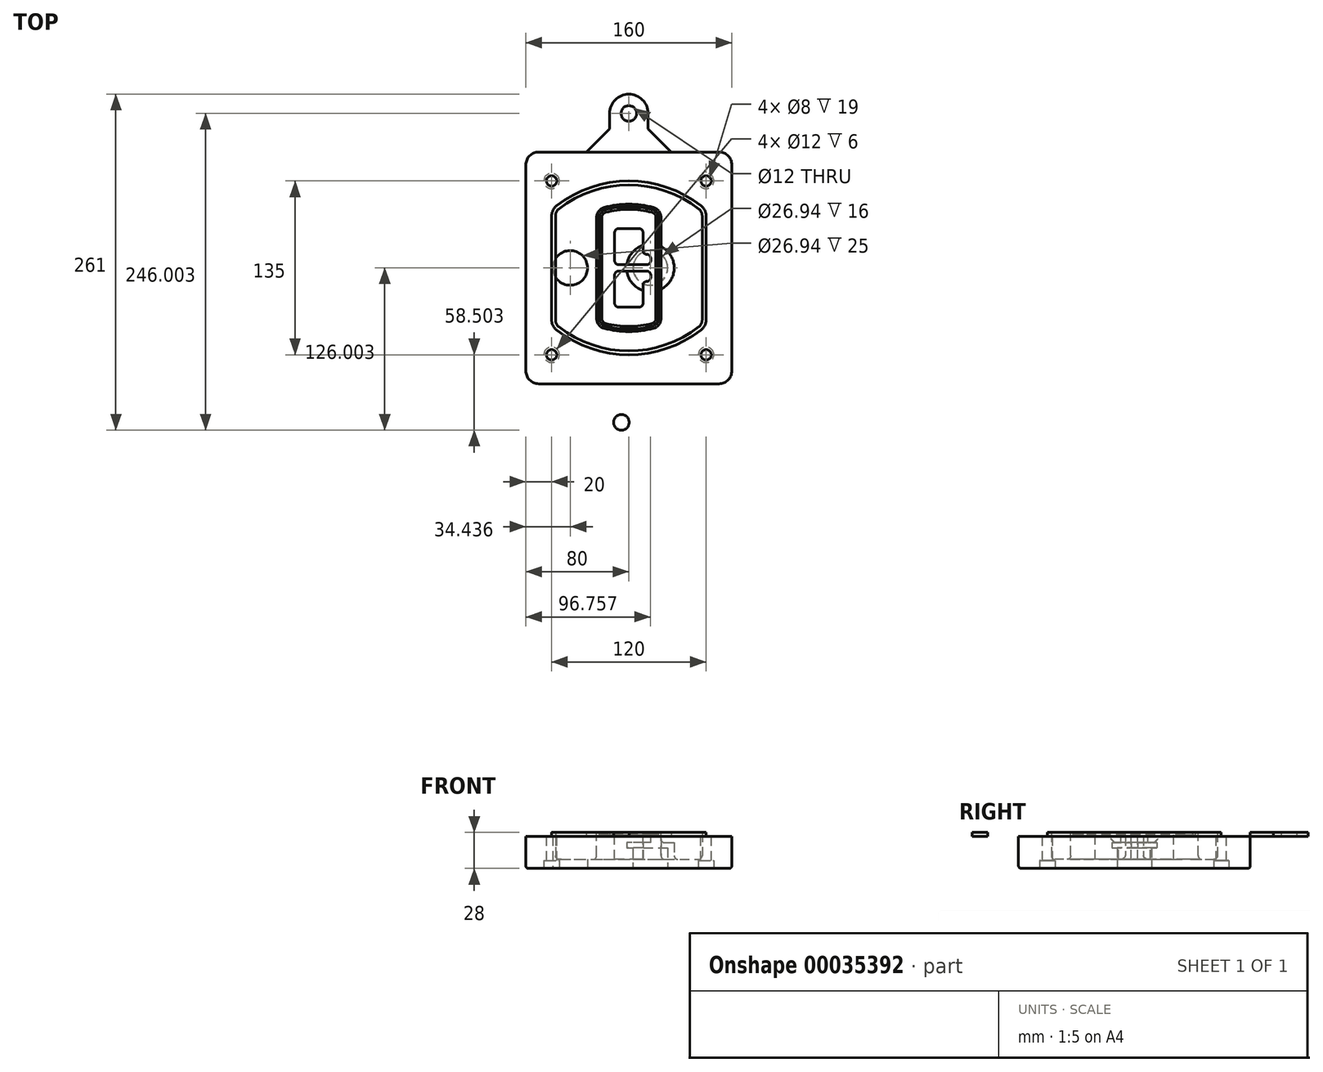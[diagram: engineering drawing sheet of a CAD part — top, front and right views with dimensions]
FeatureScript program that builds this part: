
annotation { "Feature Type Name" : "Feature", "Feature Type Description" : "" }
export const myFeature = defineFeature(function(context is Context, id is Id, definition is map)
    precondition{}
    {
        {
            var Q0;
            Q0=qCreatedBy(makeId("Top.planeOp"),FACE);
            var sketch = newSketch(context, id + "F0", { "sketchPlane" : qUnion([Q0])});
            skPoint(sketch, "E0.rect.middle", {"position": v(0, 0) * mm});
            skLineSegment(sketch, "E1.bottom", {"start": v(24.05, 28.38) * mm, "end": v(164.05, 28.38) * mm});
            skLineSegment(sketch, "E1.top", {"start": v(24.05, 208.38) * mm, "end": v(164.05, 208.38) * mm});
            skLineSegment(sketch, "E1.left", {"start": v(14.05, 38.38) * mm, "end": v(14.05, 198.38) * mm});
            skLineSegment(sketch, "E1.right", {"start": v(174.05, 38.38) * mm, "end": v(174.05, 198.38) * mm});
            skLineSegment(sketch, "E2", {"start": v(14.05, 208.38) * mm, "end": v(174.05, 28.38) * mm, "construction": true});
            skLineSegment(sketch, "E3", {"start": v(174.05, 208.38) * mm, "end": v(14.05, 28.38) * mm, "construction": true});
            skCircle(sketch, "E4", {"center": v(34.05, 185.88) * mm, "radius": 4 * mm});
            skCircle(sketch, "E5", {"center": v(154.05, 185.88) * mm, "radius": 4 * mm});
            skCircle(sketch, "E6", {"center": v(154.05, 50.88) * mm, "radius": 4 * mm});
            skCircle(sketch, "E7", {"center": v(34.05, 50.88) * mm, "radius": 4 * mm});
            skLineSegment(sketch, "E8", {"start": v(34.05, 185.88) * mm, "end": v(154.05, 185.88) * mm, "construction": true});
            skLineSegment(sketch, "E9", {"start": v(154.05, 185.88) * mm, "end": v(154.05, 50.88) * mm, "construction": true});
            skLineSegment(sketch, "E10", {"start": v(154.05, 50.88) * mm, "end": v(34.05, 50.88) * mm, "construction": true});
            skLineSegment(sketch, "E11", {"start": v(34.05, 50.88) * mm, "end": v(34.05, 185.88) * mm, "construction": true});
            skLineSegment(sketch, "E12", {"start": v(34.05, 158.68) * mm, "end": v(34.05, 78.09) * mm});
            skLineSegment(sketch, "E13", {"start": v(154.05, 158.68) * mm, "end": v(154.05, 78.09) * mm});
            skArc(sketch, "E14", {"start": v(150.2, 166.56) * mm, "mid": v(94.05, 185.88) * mm, "end": v(37.9, 166.56) * mm});
            skArc(sketch, "E15", {"start": v(37.9, 70.2) * mm, "mid": v(94.05, 50.88) * mm, "end": v(150.2, 70.2) * mm});
            skLineSegment(sketch, "E16", {"start": v(34.05, 118.38) * mm, "end": v(154.05, 118.38) * mm, "construction": true});
            skPoint(sketch, "E17.visualSharp", {"position": v(34.05, 73.38) * mm});
            skArc(sketch, "E17.filletArc", {"start": v(34.05, 78.09) * mm, "mid": v(35.06, 73.7) * mm, "end": v(37.9, 70.2) * mm});
            skPoint(sketch, "E18.visualSharp", {"position": v(34.05, 163.38) * mm});
            skArc(sketch, "E18.filletArc", {"start": v(37.9, 166.56) * mm, "mid": v(35.06, 163.06) * mm, "end": v(34.05, 158.68) * mm});
            skPoint(sketch, "E19.visualSharp", {"position": v(154.05, 163.38) * mm});
            skArc(sketch, "E19.filletArc", {"start": v(154.05, 158.68) * mm, "mid": v(153.04, 163.06) * mm, "end": v(150.2, 166.56) * mm});
            skPoint(sketch, "E20.visualSharp", {"position": v(154.05, 73.38) * mm});
            skArc(sketch, "E20.filletArc", {"start": v(150.2, 70.2) * mm, "mid": v(153.04, 73.7) * mm, "end": v(154.05, 78.09) * mm});
            skPoint(sketch, "E21.visualSharp", {"position": v(14.05, 208.38) * mm});
            skArc(sketch, "E21.filletArc", {"start": v(24.05, 208.38) * mm, "mid": v(16.98, 205.45) * mm, "end": v(14.05, 198.38) * mm});
            skPoint(sketch, "E22.visualSharp", {"position": v(174.05, 208.38) * mm});
            skArc(sketch, "E22.filletArc", {"start": v(174.05, 198.38) * mm, "mid": v(171.12, 205.45) * mm, "end": v(164.05, 208.38) * mm});
            skPoint(sketch, "E23.visualSharp", {"position": v(174.05, 28.38) * mm});
            skArc(sketch, "E23.filletArc", {"start": v(164.05, 28.38) * mm, "mid": v(171.12, 31.31) * mm, "end": v(174.05, 38.38) * mm});
            skPoint(sketch, "E24.visualSharp", {"position": v(14.05, 28.38) * mm});
            skArc(sketch, "E24.filletArc", {"start": v(14.05, 38.38) * mm, "mid": v(16.98, 31.31) * mm, "end": v(24.05, 28.38) * mm});
            skArc(sketch, "E25.0", {"start": v(151.05, 158.68) * mm, "mid": v(150.34, 161.75) * mm, "end": v(148.36, 164.2) * mm});
            skLineSegment(sketch, "E25.1", {"start": v(151.05, 158.68) * mm, "end": v(151.05, 78.09) * mm});
            skArc(sketch, "E25.2", {"start": v(148.36, 72.57) * mm, "mid": v(150.34, 75.02) * mm, "end": v(151.05, 78.09) * mm});
            skArc(sketch, "E25.3", {"start": v(39.74, 72.57) * mm, "mid": v(94.05, 53.88) * mm, "end": v(148.36, 72.57) * mm});
            skArc(sketch, "E25.4", {"start": v(37.05, 78.09) * mm, "mid": v(37.76, 75.02) * mm, "end": v(39.74, 72.57) * mm});
            skArc(sketch, "E25.5", {"start": v(148.36, 164.2) * mm, "mid": v(94.05, 182.88) * mm, "end": v(39.74, 164.2) * mm});
            skLineSegment(sketch, "E25.6", {"start": v(37.05, 158.68) * mm, "end": v(37.05, 78.09) * mm});
            skArc(sketch, "E25.7", {"start": v(39.74, 164.2) * mm, "mid": v(37.76, 161.75) * mm, "end": v(37.05, 158.68) * mm});
            skArc(sketch, "E26.0", {"start": v(35.43, 169.71) * mm, "mid": v(31.47, 164.82) * mm, "end": v(30.05, 158.68) * mm});
            skArc(sketch, "E26.1", {"start": v(152.67, 169.71) * mm, "mid": v(94.05, 189.88) * mm, "end": v(35.43, 169.71) * mm});
            skArc(sketch, "E26.2", {"start": v(158.05, 158.68) * mm, "mid": v(156.63, 164.82) * mm, "end": v(152.67, 169.71) * mm});
            skLineSegment(sketch, "E26.3", {"start": v(158.05, 158.68) * mm, "end": v(158.05, 78.09) * mm});
            skArc(sketch, "E26.4", {"start": v(152.67, 67.05) * mm, "mid": v(156.63, 71.95) * mm, "end": v(158.05, 78.09) * mm});
            skLineSegment(sketch, "E26.5", {"start": v(30.05, 158.68) * mm, "end": v(30.05, 78.09) * mm});
            skArc(sketch, "E26.6", {"start": v(35.43, 67.05) * mm, "mid": v(94.05, 46.88) * mm, "end": v(152.67, 67.05) * mm});
            skArc(sketch, "E26.7", {"start": v(30.05, 78.09) * mm, "mid": v(31.47, 71.95) * mm, "end": v(35.43, 67.05) * mm});
            skSolve(sketch);
        }
        {
            var Q0;
            Q0=makeQuery(id+"F0.imprint","IMPRINT",FACE,{"disambiguationData":[TD([[makeQuery(id+"F0.imprint","IMPRINT",EDGE,{"derivedFrom":sQuery(id+"F0.wireOp",EDGE,"E1.bottom")}),1.0]])]});
            var Q1;
            Q1=makeQuery(id+"F0.imprint","IMPRINT",FACE,{"disambiguationData":[TD([[makeQuery(id+"F0.imprint","IMPRINT",EDGE,{"derivedFrom":sQuery(id+"F0.wireOp",EDGE,"E12")}),1.0]])]});
            var Q2;
            Q2=makeQuery(id+"F0.imprint","IMPRINT",FACE,{"disambiguationData":[TD([[makeQuery(id+"F0.imprint","IMPRINT",EDGE,{"derivedFrom":sQuery(id+"F0.wireOp",EDGE,"E25.0")}),1.0]])]});
            var Q3;
            Q3=makeQuery(id+"F0.imprint","IMPRINT",FACE,{"disambiguationData":[TD([[makeQuery(id+"F0.imprint","IMPRINT",EDGE,{"derivedFrom":sQuery(id+"F0.wireOp",EDGE,"E12")}),-1.0]])]});
            extrude(context, id + "F1", {"entities" : qUnion([Q0, Q1, Q2, Q3]), "oppositeDirection" : true, "depth" : 25 * mm});
        }
        {
            var Q0;
            Q0=makeQuery(id+"F0.imprint","IMPRINT",FACE,{"disambiguationData":[TD([[makeQuery(id+"F0.imprint","IMPRINT",EDGE,{"derivedFrom":sQuery(id+"F0.wireOp",EDGE,"E12")}),1.0]])]});
            extrude(context, id + "F2", {"entities" : qUnion([Q0]), "operationType" : NewBodyOperationType.ADD, "depth" : 3 * mm});
        }
        {
            var Q0;
            Q0=makeQuery(id+"F0.imprint","IMPRINT",FACE,{"disambiguationData":[TD([[makeQuery(id+"F0.imprint","IMPRINT",EDGE,{"derivedFrom":sQuery(id+"F0.wireOp",EDGE,"E25.0")}),1.0]])]});
            extrude(context, id + "F3", {"entities" : qUnion([Q0]), "operationType" : NewBodyOperationType.REMOVE, "oppositeDirection" : true, "depth" : 18 * mm});
        }
        {
            var Q0;
            Q0=makeQuery(id+"F2.opExtrude","CAP_FACE",FACE,{"disambiguationData":[OSD([sQuery(id+"F0.wireOp",EDGE,"E12"),sQuery(id+"F0.wireOp",EDGE,"E13"),sQuery(id+"F0.wireOp",EDGE,"E14"),sQuery(id+"F0.wireOp",EDGE,"E15"),sQuery(id+"F0.wireOp",EDGE,"E17.filletArc"),sQuery(id+"F0.wireOp",EDGE,"E18.filletArc"),sQuery(id+"F0.wireOp",EDGE,"E19.filletArc"),sQuery(id+"F0.wireOp",EDGE,"E20.filletArc"),sQuery(id+"F0.wireOp",EDGE,"E25.0"),sQuery(id+"F0.wireOp",EDGE,"E25.1"),sQuery(id+"F0.wireOp",EDGE,"E25.2"),sQuery(id+"F0.wireOp",EDGE,"E25.3"),sQuery(id+"F0.wireOp",EDGE,"E25.4"),sQuery(id+"F0.wireOp",EDGE,"E25.5"),sQuery(id+"F0.wireOp",EDGE,"E25.6"),sQuery(id+"F0.wireOp",EDGE,"E25.7")])],"isStart":false});
            var sketch = newSketch(context, id + "F4", { "sketchPlane" : qUnion([Q0])});
            skArc(sketch, "E27.0", {"start": v(74.97, 71.41) * mm, "mid": v(94.05, 68.88) * mm, "end": v(113.13, 71.41) * mm});
            skArc(sketch, "E28.0", {"start": v(113.13, 165.35) * mm, "mid": v(94.05, 167.88) * mm, "end": v(74.97, 165.35) * mm});
            skLineSegment(sketch, "E29", {"start": v(69.05, 157.63) * mm, "end": v(69.05, 79.14) * mm});
            skLineSegment(sketch, "E30", {"start": v(119.05, 157.63) * mm, "end": v(119.05, 79.14) * mm});
            skLineSegment(sketch, "E31", {"start": v(69.05, 163.48) * mm, "end": v(119.05, 163.48) * mm, "construction": true});
            skLineSegment(sketch, "E32", {"start": v(69.05, 73.28) * mm, "end": v(119.05, 73.28) * mm, "construction": true});
            skPoint(sketch, "E33.visualSharp", {"position": v(69.05, 163.48) * mm});
            skArc(sketch, "E33.filletArc", {"start": v(74.97, 165.35) * mm, "mid": v(70.7, 162.5) * mm, "end": v(69.05, 157.63) * mm});
            skPoint(sketch, "E34.visualSharp", {"position": v(119.05, 163.48) * mm});
            skArc(sketch, "E34.filletArc", {"start": v(119.05, 157.63) * mm, "mid": v(117.4, 162.5) * mm, "end": v(113.13, 165.35) * mm});
            skPoint(sketch, "E35.visualSharp", {"position": v(119.05, 73.28) * mm});
            skArc(sketch, "E35.filletArc", {"start": v(113.13, 71.41) * mm, "mid": v(117.4, 74.27) * mm, "end": v(119.05, 79.14) * mm});
            skPoint(sketch, "E36.visualSharp", {"position": v(69.05, 73.28) * mm});
            skArc(sketch, "E36.filletArc", {"start": v(69.05, 79.14) * mm, "mid": v(70.7, 74.27) * mm, "end": v(74.97, 71.41) * mm});
            skArc(sketch, "E37.0", {"start": v(148.36, 164.2) * mm, "mid": v(94.05, 182.88) * mm, "end": v(39.74, 164.2) * mm});
            skArc(sketch, "E37.1", {"start": v(39.74, 164.2) * mm, "mid": v(37.76, 161.75) * mm, "end": v(37.05, 158.68) * mm});
            skLineSegment(sketch, "E37.2", {"start": v(37.05, 158.68) * mm, "end": v(37.05, 78.09) * mm});
            skArc(sketch, "E37.3", {"start": v(37.05, 78.09) * mm, "mid": v(37.76, 75.02) * mm, "end": v(39.74, 72.57) * mm});
            skArc(sketch, "E37.4", {"start": v(39.74, 72.57) * mm, "mid": v(94.05, 53.88) * mm, "end": v(148.36, 72.57) * mm});
            skArc(sketch, "E37.5", {"start": v(148.36, 72.57) * mm, "mid": v(150.34, 75.02) * mm, "end": v(151.05, 78.09) * mm});
            skLineSegment(sketch, "E37.6", {"start": v(151.05, 158.68) * mm, "end": v(151.05, 78.09) * mm});
            skArc(sketch, "E37.7", {"start": v(151.05, 158.68) * mm, "mid": v(150.34, 161.75) * mm, "end": v(148.36, 164.2) * mm});
            skLineSegment(sketch, "E38.0", {"start": v(117.05, 157.63) * mm, "end": v(117.05, 79.14) * mm});
            skArc(sketch, "E38.1", {"start": v(112.61, 73.34) * mm, "mid": v(115.81, 75.49) * mm, "end": v(117.05, 79.14) * mm});
            skArc(sketch, "E38.2", {"start": v(75.49, 73.34) * mm, "mid": v(94.05, 70.88) * mm, "end": v(112.61, 73.34) * mm});
            skArc(sketch, "E38.3", {"start": v(71.05, 79.14) * mm, "mid": v(72.29, 75.49) * mm, "end": v(75.49, 73.34) * mm});
            skLineSegment(sketch, "E38.4", {"start": v(71.05, 157.63) * mm, "end": v(71.05, 79.14) * mm});
            skArc(sketch, "E38.5", {"start": v(117.05, 157.63) * mm, "mid": v(115.81, 161.28) * mm, "end": v(112.61, 163.42) * mm});
            skArc(sketch, "E38.6", {"start": v(75.49, 163.42) * mm, "mid": v(72.29, 161.28) * mm, "end": v(71.05, 157.63) * mm});
            skArc(sketch, "E38.7", {"start": v(112.61, 163.42) * mm, "mid": v(94.05, 165.88) * mm, "end": v(75.49, 163.42) * mm});
            skArc(sketch, "E39.0", {"start": v(115.05, 157.63) * mm, "mid": v(114.23, 160.06) * mm, "end": v(112.1, 161.5) * mm});
            skLineSegment(sketch, "E39.1", {"start": v(115.05, 157.63) * mm, "end": v(115.05, 79.14) * mm});
            skArc(sketch, "E39.2", {"start": v(112.1, 75.27) * mm, "mid": v(114.23, 76.7) * mm, "end": v(115.05, 79.14) * mm});
            skArc(sketch, "E39.3", {"start": v(76, 75.27) * mm, "mid": v(94.05, 72.88) * mm, "end": v(112.1, 75.27) * mm});
            skArc(sketch, "E39.4", {"start": v(73.05, 79.14) * mm, "mid": v(73.87, 76.7) * mm, "end": v(76, 75.27) * mm});
            skArc(sketch, "E39.5", {"start": v(112.1, 161.5) * mm, "mid": v(94.05, 163.88) * mm, "end": v(76, 161.5) * mm});
            skLineSegment(sketch, "E39.6", {"start": v(73.05, 157.63) * mm, "end": v(73.05, 79.14) * mm});
            skArc(sketch, "E39.7", {"start": v(76, 161.5) * mm, "mid": v(73.87, 160.06) * mm, "end": v(73.05, 157.63) * mm});
            skLineSegment(sketch, "E40", {"start": v(69.05, 118.38) * mm, "end": v(119.05, 118.38) * mm, "construction": true});
            skLineSegment(sketch, "E41", {"start": v(83.05, 123.88) * mm, "end": v(83.05, 145.88) * mm});
            skLineSegment(sketch, "E42", {"start": v(86.05, 148.88) * mm, "end": v(102.05, 148.88) * mm});
            skLineSegment(sketch, "E43", {"start": v(105.05, 145.88) * mm, "end": v(105.05, 131.88) * mm});
            skLineSegment(sketch, "E44", {"start": v(108.05, 128.88) * mm, "end": v(108.05, 128.88) * mm});
            skLineSegment(sketch, "E45", {"start": v(111.05, 125.88) * mm, "end": v(111.05, 123.88) * mm});
            skLineSegment(sketch, "E46", {"start": v(108.05, 120.88) * mm, "end": v(86.05, 120.88) * mm});
            skPoint(sketch, "E47.visualSharp", {"position": v(83.05, 148.88) * mm});
            skArc(sketch, "E47.filletArc", {"start": v(86.05, 148.88) * mm, "mid": v(83.93, 148) * mm, "end": v(83.05, 145.88) * mm});
            skPoint(sketch, "E48.visualSharp", {"position": v(105.05, 148.88) * mm});
            skArc(sketch, "E48.filletArc", {"start": v(105.05, 145.88) * mm, "mid": v(104.17, 148) * mm, "end": v(102.05, 148.88) * mm});
            skPoint(sketch, "E49.visualSharp", {"position": v(105.05, 128.88) * mm});
            skArc(sketch, "E49.filletArc", {"start": v(105.05, 131.88) * mm, "mid": v(105.93, 129.76) * mm, "end": v(108.05, 128.88) * mm});
            skPoint(sketch, "E50.visualSharp", {"position": v(111.05, 128.88) * mm});
            skArc(sketch, "E50.filletArc", {"start": v(111.05, 125.88) * mm, "mid": v(110.17, 128) * mm, "end": v(108.05, 128.88) * mm});
            skPoint(sketch, "E51.visualSharp", {"position": v(111.05, 120.88) * mm});
            skArc(sketch, "E51.filletArc", {"start": v(108.05, 120.88) * mm, "mid": v(110.17, 121.76) * mm, "end": v(111.05, 123.88) * mm});
            skPoint(sketch, "E52.visualSharp", {"position": v(83.05, 120.88) * mm});
            skArc(sketch, "E52.filletArc", {"start": v(83.05, 123.88) * mm, "mid": v(83.93, 121.76) * mm, "end": v(86.05, 120.88) * mm});
            skLineSegment(sketch, "E53.0.MirrorCS", {"start": v(108.05, 115.88) * mm, "end": v(86.05, 115.88) * mm});
            skArc(sketch, "E54.0.MirrorCS", {"start": v(83.05, 112.88) * mm, "mid": v(83.93, 115) * mm, "end": v(86.05, 115.88) * mm});
            skLineSegment(sketch, "E55.0.MirrorCS", {"start": v(83.05, 112.88) * mm, "end": v(83.05, 90.88) * mm});
            skArc(sketch, "E56.0.MirrorCS", {"start": v(86.05, 87.88) * mm, "mid": v(83.93, 88.76) * mm, "end": v(83.05, 90.88) * mm});
            skLineSegment(sketch, "E57.0.MirrorCS", {"start": v(86.05, 87.88) * mm, "end": v(102.05, 87.88) * mm});
            skArc(sketch, "E58.0.MirrorCS", {"start": v(105.05, 90.88) * mm, "mid": v(104.17, 88.76) * mm, "end": v(102.05, 87.88) * mm});
            skLineSegment(sketch, "E59.0.MirrorCS", {"start": v(105.05, 90.88) * mm, "end": v(105.05, 104.88) * mm});
            skArc(sketch, "E60.0.MirrorCS", {"start": v(105.05, 104.88) * mm, "mid": v(105.93, 107) * mm, "end": v(108.05, 107.88) * mm});
            skArc(sketch, "E61.0.MirrorCS", {"start": v(111.05, 110.88) * mm, "mid": v(110.17, 108.76) * mm, "end": v(108.05, 107.88) * mm});
            skLineSegment(sketch, "E62.0.MirrorCS", {"start": v(111.05, 110.88) * mm, "end": v(111.05, 112.88) * mm});
            skArc(sketch, "E63.0.MirrorCS", {"start": v(108.05, 115.88) * mm, "mid": v(110.17, 115) * mm, "end": v(111.05, 112.88) * mm});
            skSolve(sketch);
        }
        {
            var Q0;
            Q0=makeQuery(id+"F4.imprint","IMPRINT",FACE,{"disambiguationData":[TD([[makeQuery(id+"F4.imprint","IMPRINT",EDGE,{"derivedFrom":sQuery(id+"F4.wireOp",EDGE,"E27.0")}),1.0]])]});
            var Q1;
            Q1=makeQuery(id+"F4.imprint","IMPRINT",FACE,{"disambiguationData":[TD([[makeQuery(id+"F4.imprint","IMPRINT",EDGE,{"derivedFrom":sQuery(id+"F4.wireOp",EDGE,"E38.0")}),-1.0]])]});
            var Q2;
            Q2=makeQuery(id+"F4.imprint","IMPRINT",FACE,{"disambiguationData":[TD([[makeQuery(id+"F4.imprint","IMPRINT",EDGE,{"derivedFrom":sQuery(id+"F4.wireOp",EDGE,"E39.0")}),1.0]])]});
            extrude(context, id + "F5", {"entities" : qUnion([Q0, Q1, Q2]), "operationType" : NewBodyOperationType.ADD, "endBound" : BoundingType.UP_TO_NEXT, "oppositeDirection" : true, "depth" : 25 * mm});
        }
        {
            var Q0;
            Q0=makeQuery(id+"F4.imprint","IMPRINT",FACE,{"disambiguationData":[TD([[makeQuery(id+"F4.imprint","IMPRINT",EDGE,{"derivedFrom":sQuery(id+"F4.wireOp",EDGE,"E38.0")}),-1.0]])]});
            extrude(context, id + "F6", {"entities" : qUnion([Q0]), "operationType" : NewBodyOperationType.REMOVE, "oppositeDirection" : true, "depth" : 2 * mm});
        }
        {
            var Q0;
            Q0=makeQuery(id+"F1.opExtrude","CAP_FACE",FACE,{"disambiguationData":[OSD([sQuery(id+"F0.wireOp",EDGE,"E1.bottom"),sQuery(id+"F0.wireOp",EDGE,"E1.top"),sQuery(id+"F0.wireOp",EDGE,"E1.left"),sQuery(id+"F0.wireOp",EDGE,"E1.right"),sQuery(id+"F0.wireOp",EDGE,"E4"),sQuery(id+"F0.wireOp",EDGE,"E5"),sQuery(id+"F0.wireOp",EDGE,"E6"),sQuery(id+"F0.wireOp",EDGE,"E7"),sQuery(id+"F0.wireOp",EDGE,"E21.filletArc"),sQuery(id+"F0.wireOp",EDGE,"E22.filletArc"),sQuery(id+"F0.wireOp",EDGE,"E23.filletArc"),sQuery(id+"F0.wireOp",EDGE,"E24.filletArc")])],"isStart":false});
            var sketch = newSketch(context, id + "F7", { "sketchPlane" : qUnion([Q0])});
            skCircle(sketch, "E64", {"center": v(110.8, -118.38) * mm, "radius": 13.47 * mm});
            skCircle(sketch, "E65", {"center": v(48.49, -118.38) * mm, "radius": 13.47 * mm});
            skLineSegment(sketch, "E66", {"start": v(174.05, -118.38) * mm, "end": v(14.05, -118.38) * mm});
            skCircle(sketch, "E67", {"center": v(110.8, -118.38) * mm, "radius": 18.47 * mm});
            skCircle(sketch, "E68", {"center": v(154.05, -185.88) * mm, "radius": 6 * mm});
            skCircle(sketch, "E69", {"center": v(34.05, -185.88) * mm, "radius": 6 * mm});
            skCircle(sketch, "E70", {"center": v(34.05, -50.88) * mm, "radius": 6 * mm});
            skCircle(sketch, "E71", {"center": v(154.05, -50.88) * mm, "radius": 6 * mm});
            skSolve(sketch);
        }
        {
            var Q0;
            {var subQ1=sQuery(id+"F7.wireOp",EDGE,"E66");var subQ4=sQuery(id+"F7.wireOp",EDGE,"E64");var subQ6=makeQuery(id+"F7.imprint","INTERSECT",VERTEX,{"disambiguationData":[OD(0.0)],"derivedFrom":[subQ4,subQ1]});Q0=makeQuery(id+"F7.imprint","IMPRINT",FACE,{"disambiguationData":[TD([[makeQuery(id+"F7.imprint","IMPRINT",EDGE,{"disambiguationData":[TD([[subQ6,-1.0]])],"derivedFrom":subQ4}),-1.0]])]});}
            var Q1;
            {var subQ0=sQuery(id+"F7.wireOp",EDGE,"E66");var subQ1=sQuery(id+"F7.wireOp",EDGE,"E64");var subQ3=makeQuery(id+"F7.imprint","INTERSECT",VERTEX,{"disambiguationData":[OD(0.0)],"derivedFrom":[subQ1,subQ0]});Q1=makeQuery(id+"F7.imprint","IMPRINT",FACE,{"disambiguationData":[TD([[makeQuery(id+"F7.imprint","IMPRINT",EDGE,{"disambiguationData":[TD([[subQ3,-1.0]])],"derivedFrom":subQ1}),1.0]])]});}
            var Q2;
            {var subQ0=sQuery(id+"F7.wireOp",EDGE,"E66");var subQ1=sQuery(id+"F7.wireOp",EDGE,"E64");var subQ3=makeQuery(id+"F7.imprint","INTERSECT",VERTEX,{"disambiguationData":[OD(0.0)],"derivedFrom":[subQ1,subQ0]});Q2=makeQuery(id+"F7.imprint","IMPRINT",FACE,{"disambiguationData":[TD([[makeQuery(id+"F7.imprint","IMPRINT",EDGE,{"disambiguationData":[TD([[subQ3,1.0]])],"derivedFrom":subQ1}),1.0]])]});}
            var Q3;
            {var subQ1=sQuery(id+"F7.wireOp",EDGE,"E66");var subQ4=sQuery(id+"F7.wireOp",EDGE,"E64");var subQ6=makeQuery(id+"F7.imprint","INTERSECT",VERTEX,{"disambiguationData":[OD(0.0)],"derivedFrom":[subQ4,subQ1]});Q3=makeQuery(id+"F7.imprint","IMPRINT",FACE,{"disambiguationData":[TD([[makeQuery(id+"F7.imprint","IMPRINT",EDGE,{"disambiguationData":[TD([[subQ6,1.0]])],"derivedFrom":subQ4}),-1.0]])]});}
            extrude(context, id + "F8", {"entities" : qUnion([Q0, Q1, Q2, Q3]), "operationType" : NewBodyOperationType.ADD, "oppositeDirection" : true, "depth" : 20 * mm});
        }
        {
            var Q0;
            {var subQ0=sQuery(id+"F7.wireOp",EDGE,"E66");var subQ1=sQuery(id+"F7.wireOp",EDGE,"E64");var subQ3=makeQuery(id+"F7.imprint","INTERSECT",VERTEX,{"disambiguationData":[OD(0.0)],"derivedFrom":[subQ1,subQ0]});Q0=makeQuery(id+"F7.imprint","IMPRINT",FACE,{"disambiguationData":[TD([[makeQuery(id+"F7.imprint","IMPRINT",EDGE,{"disambiguationData":[TD([[subQ3,-1.0]])],"derivedFrom":subQ1}),1.0]])]});}
            var Q1;
            {var subQ0=sQuery(id+"F7.wireOp",EDGE,"E66");var subQ1=sQuery(id+"F7.wireOp",EDGE,"E64");var subQ3=makeQuery(id+"F7.imprint","INTERSECT",VERTEX,{"disambiguationData":[OD(0.0)],"derivedFrom":[subQ1,subQ0]});Q1=makeQuery(id+"F7.imprint","IMPRINT",FACE,{"disambiguationData":[TD([[makeQuery(id+"F7.imprint","IMPRINT",EDGE,{"disambiguationData":[TD([[subQ3,1.0]])],"derivedFrom":subQ1}),1.0]])]});}
            extrude(context, id + "F9", {"entities" : qUnion([Q0, Q1]), "operationType" : NewBodyOperationType.REMOVE, "oppositeDirection" : true, "depth" : 16 * mm});
        }
        {
            var Q0;
            {var subQ0=sQuery(id+"F7.wireOp",EDGE,"E66");var subQ1=sQuery(id+"F7.wireOp",EDGE,"E65");var subQ3=makeQuery(id+"F7.imprint","INTERSECT",VERTEX,{"disambiguationData":[OD(0.0)],"derivedFrom":[subQ1,subQ0]});Q0=makeQuery(id+"F7.imprint","IMPRINT",FACE,{"disambiguationData":[TD([[makeQuery(id+"F7.imprint","IMPRINT",EDGE,{"disambiguationData":[TD([[subQ3,-1.0]])],"derivedFrom":subQ1}),1.0]])]});}
            var Q1;
            {var subQ0=sQuery(id+"F7.wireOp",EDGE,"E66");var subQ1=sQuery(id+"F7.wireOp",EDGE,"E65");var subQ3=makeQuery(id+"F7.imprint","INTERSECT",VERTEX,{"disambiguationData":[OD(0.0)],"derivedFrom":[subQ1,subQ0]});Q1=makeQuery(id+"F7.imprint","IMPRINT",FACE,{"disambiguationData":[TD([[makeQuery(id+"F7.imprint","IMPRINT",EDGE,{"disambiguationData":[TD([[subQ3,1.0]])],"derivedFrom":subQ1}),1.0]])]});}
            extrude(context, id + "F10", {"entities" : qUnion([Q0, Q1]), "operationType" : NewBodyOperationType.REMOVE, "oppositeDirection" : true, "depth" : 25 * mm});
        }
        {
            var Q0;
            Q0=makeQuery(id+"F7.imprint","IMPRINT",FACE,{"disambiguationData":[TD([[makeQuery(id+"F7.imprint","IMPRINT",EDGE,{"derivedFrom":sQuery(id+"F7.wireOp",EDGE,"E68")}),1.0]])]});
            var Q1;
            Q1=makeQuery(id+"F7.imprint","IMPRINT",FACE,{"disambiguationData":[TD([[makeQuery(id+"F7.imprint","IMPRINT",EDGE,{"derivedFrom":makeQuery(id+"F1.opExtrude","CAP_EDGE",EDGE,{"disambiguationData":[OSD([sQuery(id+"F0.wireOp",EDGE,"E5")])],"isStart":false})}),-1.0]])]});
            var Q2;
            Q2=makeQuery(id+"F7.imprint","IMPRINT",FACE,{"disambiguationData":[TD([[makeQuery(id+"F7.imprint","IMPRINT",EDGE,{"derivedFrom":sQuery(id+"F7.wireOp",EDGE,"E69")}),1.0]])]});
            var Q3;
            Q3=makeQuery(id+"F7.imprint","IMPRINT",FACE,{"disambiguationData":[TD([[makeQuery(id+"F7.imprint","IMPRINT",EDGE,{"derivedFrom":makeQuery(id+"F1.opExtrude","CAP_EDGE",EDGE,{"disambiguationData":[OSD([sQuery(id+"F0.wireOp",EDGE,"E4")])],"isStart":false})}),-1.0]])]});
            var Q4;
            Q4=makeQuery(id+"F7.imprint","IMPRINT",FACE,{"disambiguationData":[TD([[makeQuery(id+"F7.imprint","IMPRINT",EDGE,{"derivedFrom":sQuery(id+"F7.wireOp",EDGE,"E70")}),1.0]])]});
            var Q5;
            Q5=makeQuery(id+"F7.imprint","IMPRINT",FACE,{"disambiguationData":[TD([[makeQuery(id+"F7.imprint","IMPRINT",EDGE,{"derivedFrom":makeQuery(id+"F1.opExtrude","CAP_EDGE",EDGE,{"disambiguationData":[OSD([sQuery(id+"F0.wireOp",EDGE,"E7")])],"isStart":false})}),-1.0]])]});
            var Q6;
            Q6=makeQuery(id+"F7.imprint","IMPRINT",FACE,{"disambiguationData":[TD([[makeQuery(id+"F7.imprint","IMPRINT",EDGE,{"derivedFrom":sQuery(id+"F7.wireOp",EDGE,"E71")}),1.0]])]});
            var Q7;
            Q7=makeQuery(id+"F7.imprint","IMPRINT",FACE,{"disambiguationData":[TD([[makeQuery(id+"F7.imprint","IMPRINT",EDGE,{"derivedFrom":makeQuery(id+"F1.opExtrude","CAP_EDGE",EDGE,{"disambiguationData":[OSD([sQuery(id+"F0.wireOp",EDGE,"E6")])],"isStart":false})}),-1.0]])]});
            extrude(context, id + "F11", {"entities" : qUnion([Q0, Q1, Q2, Q3, Q4, Q5, Q6, Q7]), "operationType" : NewBodyOperationType.REMOVE, "oppositeDirection" : true, "depth" : 6 * mm});
        }
        {
            var Q0;
            Q0=makeQuery(id+"F9.boolean.opBoolean","COPY",FACE,{"derivedFrom":makeQuery(id+"F9.opExtrude","CAP_FACE",FACE,{"disambiguationData":[OSD([sQuery(id+"F7.wireOp",EDGE,"E64")])],"isStart":false})});
            var sketch = newSketch(context, id + "F12", { "sketchPlane" : qUnion([Q0])});
            skArc(sketch, "E72.0", {"start": v(105.05, -100.83) * mm, "mid": v(96.62, -106.56) * mm, "end": v(92.5, -115.88) * mm});
            skArc(sketch, "E72.1", {"start": v(92.5, -120.88) * mm, "mid": v(96.62, -130.2) * mm, "end": v(105.05, -135.93) * mm});
            skLineSegment(sketch, "E73", {"start": v(92.5, -120.88) * mm, "end": v(108.05, -120.88) * mm});
            skLineSegment(sketch, "E74.0", {"start": v(108.05, -115.88) * mm, "end": v(92.5, -115.88) * mm});
            skArc(sketch, "E74.1", {"start": v(108.05, -115.88) * mm, "mid": v(110.17, -115) * mm, "end": v(111.05, -112.88) * mm});
            skLineSegment(sketch, "E74.2", {"start": v(111.05, -110.88) * mm, "end": v(111.05, -112.88) * mm});
            skArc(sketch, "E74.3", {"start": v(111.05, -110.88) * mm, "mid": v(110.17, -108.76) * mm, "end": v(108.05, -107.88) * mm});
            skArc(sketch, "E74.4", {"start": v(105.05, -104.88) * mm, "mid": v(105.93, -107) * mm, "end": v(108.05, -107.88) * mm});
            skLineSegment(sketch, "E74.5", {"start": v(105.05, -100.83) * mm, "end": v(105.05, -104.88) * mm});
            skLineSegment(sketch, "E74.7", {"start": v(108.05, -120.88) * mm, "end": v(92.5, -120.88) * mm});
            skArc(sketch, "E74.8", {"start": v(108.05, -120.88) * mm, "mid": v(110.17, -121.76) * mm, "end": v(111.05, -123.88) * mm});
            skLineSegment(sketch, "E74.9", {"start": v(111.05, -125.88) * mm, "end": v(111.05, -123.88) * mm});
            skArc(sketch, "E74.10", {"start": v(111.05, -125.88) * mm, "mid": v(110.17, -128) * mm, "end": v(108.05, -128.88) * mm});
            skArc(sketch, "E74.11", {"start": v(105.05, -131.88) * mm, "mid": v(105.93, -129.76) * mm, "end": v(108.05, -128.88) * mm});
            skLineSegment(sketch, "E74.12", {"start": v(105.05, -135.93) * mm, "end": v(105.05, -131.88) * mm});
            skPoint(sketch, "E75.orphan", {"position": v(105.05, -145.88) * mm});
            skPoint(sketch, "E76.orphan", {"position": v(86.05, -120.88) * mm});
            skPoint(sketch, "E77.orphan", {"position": v(86.05, -115.88) * mm});
            skPoint(sketch, "E78.orphan", {"position": v(105.05, -90.88) * mm});
            skSolve(sketch);
        }
        {
            var Q0;
            {var subQ7=sQuery(id+"F12.wireOp",EDGE,"E72.0");var subQ14=sQuery(id+"F12.wireOp",EDGE,"E72.1");var subQ16=sQuery(id+"F12.wireOp",EDGE,"E74.1");var subQ18=sQuery(id+"F12.wireOp",EDGE,"E74.8");Q0=qUnion([makeQuery(id+"F12.imprint","IMPRINT",FACE,{"disambiguationData":[TD([[makeQuery(id+"F12.imprint","IMPRINT",EDGE,{"derivedFrom":subQ7}),1.0]])]}),makeQuery(id+"F12.imprint","IMPRINT",FACE,{"disambiguationData":[TD([[makeQuery(id+"F12.imprint","IMPRINT",EDGE,{"derivedFrom":subQ14}),1.0]])]}),makeQuery(id+"F12.imprint","IMPRINT",FACE,{"disambiguationData":[TD([[makeQuery(id+"F12.imprint","IMPRINT",EDGE,{"derivedFrom":subQ16}),1.0]])]}),makeQuery(id+"F12.imprint","IMPRINT",FACE,{"disambiguationData":[TD([[makeQuery(id+"F12.imprint","IMPRINT",EDGE,{"derivedFrom":subQ18}),-1.0]])]})]);}
            var Q1;
            Q1=makeQuery(id+"F5.boolean.opBoolean","SPLIT",FACE,{"disambiguationData":[TD([makeQuery(id+"F5.opExtrude","SWEPT_FACE",FACE,{"disambiguationData":[OSD([sQuery(id+"F4.wireOp",EDGE,"E41")])]})])],"derivedFrom":makeQuery(id+"F3.boolean.opBoolean","COPY",FACE,{"derivedFrom":makeQuery(id+"F3.opExtrude","CAP_FACE",FACE,{"disambiguationData":[OSD([sQuery(id+"F0.wireOp",EDGE,"E25.0"),sQuery(id+"F0.wireOp",EDGE,"E25.1"),sQuery(id+"F0.wireOp",EDGE,"E25.2"),sQuery(id+"F0.wireOp",EDGE,"E25.3"),sQuery(id+"F0.wireOp",EDGE,"E25.4"),sQuery(id+"F0.wireOp",EDGE,"E25.5"),sQuery(id+"F0.wireOp",EDGE,"E25.6"),sQuery(id+"F0.wireOp",EDGE,"E25.7")])],"isStart":false})})});
            extrude(context, id + "F13", {"entities" : qUnion([Q0]), "operationType" : NewBodyOperationType.REMOVE, "endBound" : BoundingType.UP_TO_SURFACE, "endBoundEntityFace" : qUnion([Q1]), "depth" : 25 * mm});
        }
        {
            var Q0;
            Q0=makeQuery(id+"F3.boolean.opBoolean","COPY",EDGE,{"derivedFrom":makeQuery(id+"F3.opExtrude","CAP_EDGE",EDGE,{"disambiguationData":[OSD([sQuery(id+"F0.wireOp",EDGE,"E25.6")])],"isStart":false})});
            var Q1;
            Q1=makeQuery(id+"F8.boolean.opBoolean","INTERSECT",EDGE,{"derivedFrom":[makeQuery(id+"F5.opExtrude","SWEPT_FACE",FACE,{"disambiguationData":[OSD([sQuery(id+"F4.wireOp",EDGE,"E30")])]}),makeQuery(id+"F8.opExtrude","CAP_FACE",FACE,{"disambiguationData":[OSD([sQuery(id+"F7.wireOp",EDGE,"E67")])],"isStart":false})]});
            var Q2;
            Q2=makeQuery(id+"F8.boolean.opBoolean","INTERSECT",EDGE,{"disambiguationData":[OD(1.0)],"derivedFrom":[makeQuery(id+"F5.opExtrude","SWEPT_FACE",FACE,{"disambiguationData":[OSD([sQuery(id+"F4.wireOp",EDGE,"E30")])]}),makeQuery(id+"F8.opExtrude","SWEPT_FACE",FACE,{"disambiguationData":[OSD([sQuery(id+"F7.wireOp",EDGE,"E67")])]})]});
            var Q3;
            {var subQ0=sQuery(id+"F4.wireOp",EDGE,"E30");Q3=makeQuery(id+"F8.boolean.opBoolean","SPLIT",EDGE,{"disambiguationData":[TD([makeQuery(id+"F5.opExtrude","SWEPT_FACE",FACE,{"disambiguationData":[OSD([sQuery(id+"F4.wireOp",EDGE,"E35.filletArc")])]})])],"derivedFrom":makeQuery(id+"F5.opExtrude","CAP_EDGE",EDGE,{"disambiguationData":[OSD([subQ0])],"isStart":false})});}
            var Q4;
            {var subQ0=sQuery(id+"F0.wireOp",EDGE,"E25.7");var subQ1=sQuery(id+"F0.wireOp",EDGE,"E25.1");var subQ2=sQuery(id+"F0.wireOp",EDGE,"E25.6");var subQ3=sQuery(id+"F0.wireOp",EDGE,"E25.5");var subQ4=sQuery(id+"F0.wireOp",EDGE,"E25.4");var subQ5=sQuery(id+"F0.wireOp",EDGE,"E25.0");var subQ6=sQuery(id+"F0.wireOp",EDGE,"E25.2");var subQ7=sQuery(id+"F0.wireOp",EDGE,"E25.3");Q4=makeQuery(id+"F8.boolean.opBoolean","INTERSECT",EDGE,{"derivedFrom":[makeQuery(id+"F5.boolean.opBoolean","SPLIT",FACE,{"disambiguationData":[TD([makeQuery(id+"F2.opExtrude","SWEPT_FACE",FACE,{"disambiguationData":[OSD([subQ5])]})])],"derivedFrom":makeQuery(id+"F3.boolean.opBoolean","COPY",FACE,{"derivedFrom":makeQuery(id+"F3.opExtrude","CAP_FACE",FACE,{"disambiguationData":[OSD([subQ5,subQ1,subQ6,subQ7,subQ4,subQ3,subQ2,subQ0])],"isStart":false})})}),makeQuery(id+"F8.opExtrude","SWEPT_FACE",FACE,{"disambiguationData":[OSD([sQuery(id+"F7.wireOp",EDGE,"E67")])]})]});}
            var Q5;
            Q5=makeQuery(id+"F8.boolean.opBoolean","INTERSECT",EDGE,{"disambiguationData":[OD(0.0)],"derivedFrom":[makeQuery(id+"F5.opExtrude","SWEPT_FACE",FACE,{"disambiguationData":[OSD([sQuery(id+"F4.wireOp",EDGE,"E30")])]}),makeQuery(id+"F8.opExtrude","SWEPT_FACE",FACE,{"disambiguationData":[OSD([sQuery(id+"F7.wireOp",EDGE,"E67")])]})]});
            fillet(context, id + "F14", {"entities" : qUnion([Q0, Q1, Q2, Q3, Q4, Q5]), "radius" : 3 * mm, "tangentPropagation" : true, "allowEdgeOverflow" : false});
        }
        {
            var Q0;
            Q0=makeQuery(id+"F1.opExtrude","CAP_EDGE",EDGE,{"disambiguationData":[OSD([sQuery(id+"F0.wireOp",EDGE,"E1.bottom")])],"isStart":false});
            fillet(context, id + "F15", {"entities" : qUnion([Q0]), "radius" : 2 * mm, "tangentPropagation" : true, "allowEdgeOverflow" : false});
        }
        {
            var Q0;
            {var subQ0=sQuery(id+"F0.wireOp",EDGE,"E1.bottom");var subQ1=sQuery(id+"F0.wireOp",EDGE,"E1.top");var subQ2=sQuery(id+"F0.wireOp",EDGE,"E1.left");var subQ3=sQuery(id+"F0.wireOp",EDGE,"E1.right");var subQ4=sQuery(id+"F0.wireOp",EDGE,"E4");var subQ5=sQuery(id+"F0.wireOp",EDGE,"E5");var subQ6=sQuery(id+"F0.wireOp",EDGE,"E6");var subQ7=sQuery(id+"F0.wireOp",EDGE,"E7");var subQ8=sQuery(id+"F0.wireOp",EDGE,"E21.filletArc");var subQ9=sQuery(id+"F0.wireOp",EDGE,"E22.filletArc");var subQ10=sQuery(id+"F0.wireOp",EDGE,"E23.filletArc");var subQ11=sQuery(id+"F0.wireOp",EDGE,"E24.filletArc");Q0=makeQuery(id+"F2.boolean.opBoolean","SPLIT",FACE,{"disambiguationData":[TD([makeQuery(id+"F1.opExtrude","SWEPT_FACE",FACE,{"disambiguationData":[OSD([subQ0])]})])],"derivedFrom":makeQuery(id+"F1.opExtrude","CAP_FACE",FACE,{"disambiguationData":[OSD([subQ0,subQ1,subQ2,subQ3,subQ4,subQ5,subQ6,subQ7,subQ8,subQ9,subQ10,subQ11])],"isStart":true})});}
            var sketch = newSketch(context, id + "F16", { "sketchPlane" : qUnion([Q0])});
            skLineSegment(sketch, "E79", {"start": v(94.05, 208.38) * mm, "end": v(94.05, 238.38) * mm, "construction": true});
            skCircle(sketch, "E80", {"center": v(94.05, 238.38) * mm, "radius": 6 * mm});
            skArc(sketch, "E81", {"start": v(109.05, 238.38) * mm, "mid": v(94.05, 253.38) * mm, "end": v(79.05, 238.38) * mm});
            skLineSegment(sketch, "E82", {"start": v(79.05, 238.38) * mm, "end": v(79.05, 226.38) * mm});
            skLineSegment(sketch, "E83", {"start": v(79.05, 226.38) * mm, "end": v(61.05, 208.38) * mm});
            skLineSegment(sketch, "E84.MirrorCS", {"start": v(109.05, 238.38) * mm, "end": v(109.05, 226.38) * mm});
            skLineSegment(sketch, "E85.MirrorCS", {"start": v(109.05, 226.38) * mm, "end": v(127.05, 208.38) * mm});
            skCircle(sketch, "E86.MirrorC", {"center": v(88.3, -1.62) * mm, "radius": 6 * mm});
            skArc(sketch, "E87.MirrorCS", {"start": v(103.3, -1.62) * mm, "mid": v(88.3, -16.62) * mm, "end": v(73.3, -1.62) * mm});
            skLineSegment(sketch, "E88.MirrorCS", {"start": v(73.3, -1.62) * mm, "end": v(73.3, 10.38) * mm});
            skLineSegment(sketch, "E89.MirrorCS", {"start": v(73.3, 10.38) * mm, "end": v(55.3, 28.38) * mm});
            skLineSegment(sketch, "E90.MirrorCS", {"start": v(103.3, 10.38) * mm, "end": v(121.3, 28.38) * mm});
            skLineSegment(sketch, "E91.MirrorCS", {"start": v(103.3, -1.62) * mm, "end": v(103.3, 10.38) * mm});
            skSolve(sketch);
        }
        {
            var Q0;
            Q0=makeQuery(id+"F16.imprint","IMPRINT",FACE,{"disambiguationData":[TD([[makeQuery(id+"F16.imprint","IMPRINT",EDGE,{"derivedFrom":sQuery(id+"F16.wireOp",EDGE,"E80")}),-1.0]])]});
            var Q1;
            Q1=makeQuery(id+"F16.imprint","IMPRINT",FACE,{"disambiguationData":[TD([[makeQuery(id+"F16.imprint","IMPRINT",EDGE,{"derivedFrom":sQuery(id+"F16.wireOp",EDGE,"E86.MirrorC")}),1.0]])]});
            var Q2;
            Q2=makeQuery(id+"F2.opExtrude","CAP_FACE",FACE,{"disambiguationData":[OSD([sQuery(id+"F0.wireOp",EDGE,"E12"),sQuery(id+"F0.wireOp",EDGE,"E13"),sQuery(id+"F0.wireOp",EDGE,"E14"),sQuery(id+"F0.wireOp",EDGE,"E15"),sQuery(id+"F0.wireOp",EDGE,"E17.filletArc"),sQuery(id+"F0.wireOp",EDGE,"E18.filletArc"),sQuery(id+"F0.wireOp",EDGE,"E19.filletArc"),sQuery(id+"F0.wireOp",EDGE,"E20.filletArc"),sQuery(id+"F0.wireOp",EDGE,"E25.0"),sQuery(id+"F0.wireOp",EDGE,"E25.1"),sQuery(id+"F0.wireOp",EDGE,"E25.2"),sQuery(id+"F0.wireOp",EDGE,"E25.3"),sQuery(id+"F0.wireOp",EDGE,"E25.4"),sQuery(id+"F0.wireOp",EDGE,"E25.5"),sQuery(id+"F0.wireOp",EDGE,"E25.6"),sQuery(id+"F0.wireOp",EDGE,"E25.7")])],"isStart":false});
            extrude(context, id + "F17", {"entities" : qUnion([Q0, Q1]), "endBound" : BoundingType.UP_TO_SURFACE, "endBoundEntityFace" : qUnion([Q2]), "depth" : 25 * mm});
        }
    });
